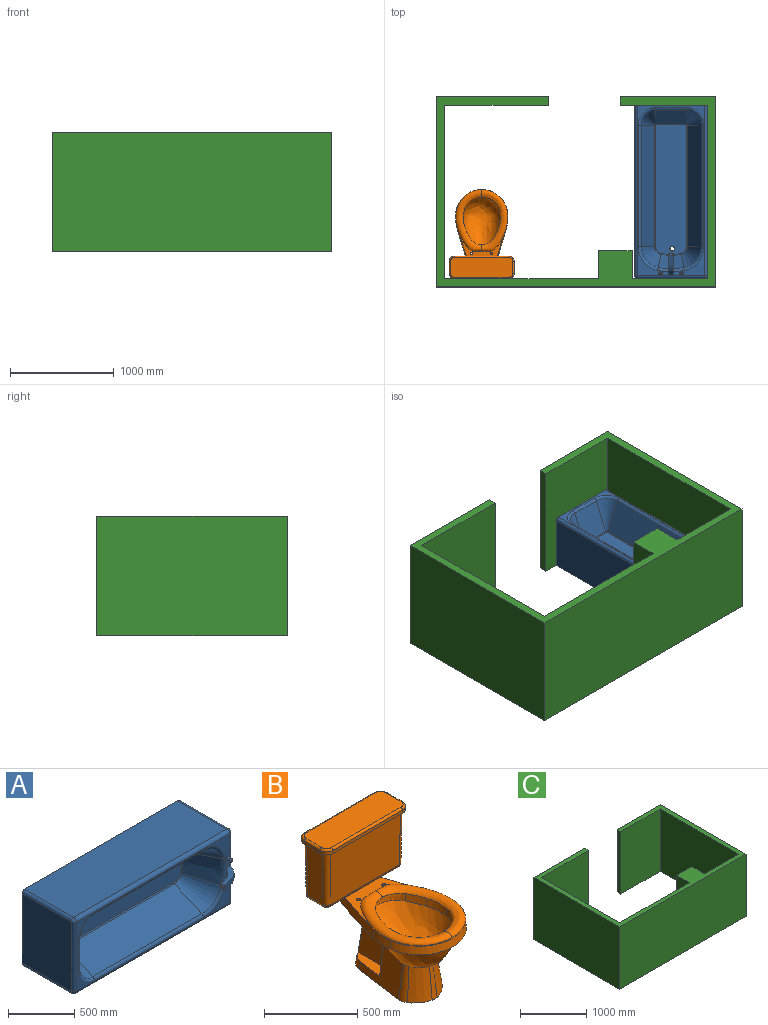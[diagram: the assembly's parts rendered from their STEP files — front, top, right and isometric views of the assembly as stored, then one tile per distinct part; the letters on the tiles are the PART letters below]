
ASSEMBLY  parts=3 mates=5
PART A: 64 faces, bbox 1708.3x711.8x712.6 mm
  f0: plane 1640x640mm, normal (0,-1,0), area 85361.7mm2, adj f16,f17,f18,f19,f20,f21,f22,f23
  f1: plane 51.88x40mm, normal (-0.3,0.95,0), area 1666.8mm2, adj f40,f41,f42,f44,f48
  f2: plane 640x525mm, normal (-1,0,0), area 336000mm2, adj f6,f18,f56,f58
  f3: plane 1640x525mm, normal (0,0,-1), area 861000mm2, adj f6,f16,f56,f62
  f4: plane 640x525mm, normal (1,0,0), area 336000mm2, adj f6,f17,f60,f62
  f5: plane 1640x525mm, normal (0,0,1), area 861000mm2, adj f6,f19,f58,f60
  f6: plane 1700x700mm, normal (0,1,0), area 1187791.8mm2, adj f2,f3,f4,f5,f36,f56,f58,f60
  f7: plane 1249.03x300.79mm, normal (0,-1,0), area 370651mm2, adj f28,f29,f30,f31,f32,f33,f34,f35
  f8: plane 1168.01x296.03mm, normal (0,-0.4,-0.92), area 377412.1mm2, adj f9,f10,f23,f30
  f9: cone r=150mm half-angle=23.6deg, axis (0,-1,0), area 39274.5mm2, adj f8,f15,f25,f28
  f10: cone r=215.58mm half-angle=23.6deg, axis (0,-1,0), area 62922.8mm2, adj f8,f11,f21,f32
  f11: cone r=608.37mm half-angle=23.6deg, axis (0,-1,0), area 72233.3mm2, adj f10,f12,f20,f34
  f12: cone r=215.58mm half-angle=23.6deg, axis (0,-1,0), area 62922.8mm2, adj f11,f13,f22,f35
  f13: plane 1168.01x296.03mm, normal (0,-0.4,0.92), area 377412.1mm2, adj f12,f14,f24,f33
  f14: cone r=150mm half-angle=23.6deg, axis (0,-1,0), area 39274.5mm2, adj f13,f15,f26,f31
  f15: plane 296.03x293.87mm, normal (0.92,-0.4,0), area 94956mm2, adj f9,f14,f27,f29
  f16: cylinder r=30mm len=1640mm, axis (1,0,0), area 77283.2mm2, adj f0,f3,f57,f63
  f17: cylinder r=30mm len=640mm, axis (0,0,1), area 30159.3mm2, adj f0,f4,f37,f61,f63
  f18: cylinder r=30mm len=640mm, axis (0,0,-1), area 30159.3mm2, adj f0,f2,f57,f59
  f19: cylinder r=30mm len=1640mm, axis (-1,0,0), area 77283.2mm2, adj f0,f5,f59,f61
  f20: torus R=627.99mm, axis (0,1,0), area 8881.1mm2, adj f0,f11,f21,f22
  f21: torus R=235.2mm, axis (0,1,0), area 10399.2mm2, adj f0,f10,f20,f23
  f22: torus R=235.2mm, axis (0,1,0), area 10399.2mm2, adj f0,f12,f20,f24
  f23: cylinder r=30mm len=1168.01mm, axis (-1,0,0), area 40590.1mm2, adj f0,f8,f21,f25
  f24: cylinder r=30mm len=1168.01mm, axis (1,0,0), area 40590.1mm2, adj f0,f13,f22,f26
  f25: torus R=169.62mm, axis (0,1,0), area 8412.1mm2, adj f0,f9,f23,f27
  f26: torus R=169.62mm, axis (0,1,0), area 8412.1mm2, adj f0,f14,f24,f27
  f27: cylinder r=30mm len=293.87mm, axis (0,0,-1), area 10212.4mm2, adj f0,f15,f25,f26
  f28: torus R=3.46mm, axis (0,-1,0), area 157.1mm2, adj f7,f9,f29,f30
  f29: cylinder r=10mm len=293.87mm, axis (0,0,-1), area 3404.1mm2, adj f7,f15,f28,f31
  f30: cylinder r=10mm len=1168.01mm, axis (-1,0,0), area 13530mm2, adj f7,f8,f28,f32
  f31: torus R=3.46mm, axis (0,-1,0), area 157.1mm2, adj f7,f14,f29,f33
  f32: torus R=69.04mm, axis (0,-1,0), area 1171mm2, adj f7,f10,f30,f34
  f33: cylinder r=10mm len=1168.01mm, axis (1,0,0), area 13530mm2, adj f7,f13,f31,f35
  f34: torus R=461.83mm, axis (0,-1,0), area 2257.2mm2, adj f7,f11,f32,f35
  f35: torus R=69.04mm, axis (0,-1,0), area 1171mm2, adj f7,f12,f33,f34
  f36: cylinder r=21.38mm len=235mm, axis (0,-1,0), area 31563.9mm2, adj f6,f7
  f37: plane 40x22.85mm, normal (0.97,-0.24,0), area 941.7mm2, adj f17,f40,f41,f43
  f38: plane 97.82x40mm, normal (0.3,-0.95,0), area 4106mm2, adj f40,f41,f43,f47
  f39: plane 20x14.29mm, normal (-0.95,-0.3,0), area 300mm2, adj f44,f45,f46,f47
  f40: plane 207.54x153.77mm, normal (0,0,-1), area 9708.8mm2, adj f0,f1,f37,f38,f42,f43,f45
  f41: plane 207.54x153.77mm, normal (0,0,1), area 9708.8mm2, adj f0,f1,f37,f38,f42,f43,f46
  f42: cylinder r=200mm len=119.6mm, axis (0,0,1), area 6516.3mm2, adj f0,f1,f40,f41
  f43: cylinder r=140mm len=99.8mm, axis (0,0,1), area 5713.6mm2, adj f37,f38,f40,f41
  f44: cylinder r=10mm len=40mm, axis (0,0,1), area 514.2mm2, adj f1,f39,f45,f46
  f45: cylinder r=10mm len=36.38mm, axis (-0.3,0.95,0), area 435.6mm2, adj f39,f40,f44,f47
  f46: cylinder r=10mm len=36.38mm, axis (0.3,-0.95,0), area 435.6mm2, adj f39,f41,f44,f47
  f47: cylinder r=10mm len=40mm, axis (0,0,1), area 514.2mm2, adj f38,f39,f45,f46
  f48: cylinder r=12.75mm len=30.37mm, axis (0.3,-0.95,0), area 1602.5mm2, adj f1,f49
  f49: plane 25.5x24.3mm, normal (-0.3,0.95,0), area 510.9mm2, adj f48
  f50: cylinder r=17.44mm len=34.88mm, axis (0,1,0), area 3286.9mm2, adj f0,f52
  f51: plane 14.88x14.88mm, normal (0,-1,0), area 173.8mm2, adj f52
  f52: torus R=7.44mm, axis (0,-1,0), area 1362.4mm2, adj f50,f51
  f53: cylinder r=17.44mm len=34.88mm, axis (0,1,0), area 3286.9mm2, adj f0,f55
  f54: plane 14.88x14.88mm, normal (0,-1,0), area 173.8mm2, adj f55
  f55: torus R=7.44mm, axis (0,-1,0), area 1362.4mm2, adj f53,f54
  f56: cylinder r=30mm len=525mm, axis (0,1,0), area 24740mm2, adj f2,f3,f6,f57
  f57: sphere r=30mm, area 1413.7mm2, adj f16,f18,f56
  f58: cylinder r=30mm len=525mm, axis (0,1,0), area 24740mm2, adj f2,f5,f6,f59
  f59: sphere r=30mm, area 1413.7mm2, adj f18,f19,f58
  f60: cylinder r=30mm len=525mm, axis (0,1,0), area 24740mm2, adj f4,f5,f6,f61
  f61: sphere r=30mm, area 1413.7mm2, adj f17,f19,f60
  f62: cylinder r=30mm len=525mm, axis (0,1,0), area 24740mm2, adj f3,f4,f6,f63
  f63: sphere r=30mm, area 1413.7mm2, adj f16,f17,f62
PART B: 178 faces, bbox 660.3x888.4x889 mm
  f0: plane 6.63x6.46mm, normal (0,0,-1), area 25mm2, adj f11,f12,f13,f110
  f1: plane 6.43x3.66mm, normal (0,0,-1), area 12.9mm2, adj f18,f108,f109
  f2: plane 6.63x6.46mm, normal (0,0,-1), area 25mm2, adj f28,f29,f30,f110
  f3: plane 6.43x3.66mm, normal (0,0,-1), area 12.9mm2, adj f35,f111,f112
  f4: plane 589.56x500.14mm, normal (0,0,-1), area 105064.3mm2, adj f5,f6,f7,f8,f9,f14,f15,f16
  f5: bspline ~589.56x250.07mm, area 66336.6mm2, adj f4,f22
  f6: plane 29.24x25.8mm, normal (0.66,-0.75,0), area 117mm2, adj f4,f7,f9,f11
  f7: cylinder r=7.5mm len=13.12mm, axis (0,0,1), area 70.7mm2, adj f4,f6,f8,f13
  f8: plane 29.24x25.8mm, normal (-0.66,0.75,0), area 117mm2, adj f4,f7,f9,f12
  f9: cylinder r=7.5mm len=13.12mm, axis (0,0,1), area 70.7mm2, adj f4,f6,f8,f10
  f10: torus R=3.5mm, axis (0,0,1), area 119.4mm2, adj f9,f11,f12,f39
  f11: cylinder r=4mm len=31.89mm, axis (0.75,0.66,0), area 245mm2, adj f0,f6,f10,f13,f39
  f12: cylinder r=4mm len=31.89mm, axis (-0.75,-0.66,0), area 245mm2, adj f0,f8,f10,f13,f39
  f13: torus R=3.5mm, axis (0,0,1), area 119.4mm2, adj f0,f7,f11,f12
  f14: cylinder r=7.5mm len=14.64mm, axis (0,0,1), area 70.7mm2, adj f4,f15,f17,f21
  f15: plane 37.1x12.02mm, normal (0.31,0.95,0), area 117mm2, adj f4,f14,f16,f20
  f16: cylinder r=7.5mm len=14.64mm, axis (0,0,1), area 70.7mm2, adj f4,f15,f17,f18
  f17: plane 37.1x12.02mm, normal (-0.31,-0.95,0), area 117mm2, adj f4,f14,f16,f19
  f18: torus R=3.5mm, axis (0,0,1), area 119.4mm2, adj f1,f16,f19,f20,f39
  f19: cylinder r=4mm len=38.34mm, axis (0.95,-0.31,0), area 245mm2, adj f17,f18,f21,f39
  f20: cylinder r=4mm len=38.34mm, axis (-0.95,0.31,0), area 245mm2, adj f15,f18,f21,f39
  f21: torus R=3.5mm, axis (0,0,1), area 119.4mm2, adj f14,f19,f20,f39
  f22: bspline ~589.56x250.07mm, area 66336.6mm2, adj f4,f5
  f23: plane 29.24x25.8mm, normal (-0.66,-0.75,0), area 117mm2, adj f4,f24,f26,f28
  f24: cylinder r=7.5mm len=13.12mm, axis (0,0,1), area 70.7mm2, adj f4,f23,f25,f30
  f25: plane 29.24x25.8mm, normal (0.66,0.75,0), area 117mm2, adj f4,f24,f26,f29
  f26: cylinder r=7.5mm len=13.12mm, axis (0,0,1), area 70.7mm2, adj f4,f23,f25,f27
  f27: torus R=3.5mm, axis (0,0,1), area 119.4mm2, adj f26,f28,f29,f39
  f28: cylinder r=4mm len=31.89mm, axis (-0.75,0.66,0), area 245mm2, adj f2,f23,f27,f30,f39
  f29: cylinder r=4mm len=31.89mm, axis (0.75,-0.66,0), area 245mm2, adj f2,f25,f27,f30,f39
  f30: torus R=3.5mm, axis (0,0,1), area 119.4mm2, adj f2,f24,f28,f29
  f31: cylinder r=7.5mm len=14.64mm, axis (0,0,1), area 70.7mm2, adj f4,f32,f34,f38
  f32: plane 37.1x12.02mm, normal (-0.31,0.95,0), area 117mm2, adj f4,f31,f33,f37
  f33: cylinder r=7.5mm len=14.64mm, axis (0,0,1), area 70.7mm2, adj f4,f32,f34,f35
  f34: plane 37.1x12.02mm, normal (0.31,-0.95,0), area 117mm2, adj f4,f31,f33,f36
  f35: torus R=3.5mm, axis (0,0,1), area 119.4mm2, adj f3,f33,f36,f37,f39
  f36: cylinder r=4mm len=38.34mm, axis (-0.95,-0.31,0), area 245mm2, adj f34,f35,f38,f39
  f37: cylinder r=4mm len=38.34mm, axis (0.95,0.31,0), area 245mm2, adj f32,f35,f38,f39
  f38: torus R=3.5mm, axis (0,0,1), area 119.4mm2, adj f31,f36,f37,f39
  f39: plane 682.07x486.65mm, normal (0,0,1), area 110534.9mm2, adj f10,f11,f12,f18,f19,f20,f21,f27
  f40: plane 601.26x191.84mm, normal (0,0,-1), area 7653mm2, adj f50,f51,f52,f53,f54,f55,f56,f57
  f41: cylinder r=49.83mm len=49.83mm, axis (0,0,1), area 1491.1mm2, adj f42,f48,f49,f65
  f42: plane 117.58x19.05mm, normal (-1,0,0), area 2239.9mm2, adj f41,f43,f49,f66
  f43: cylinder r=49.83mm len=49.83mm, axis (0,0,1), area 1491.1mm2, adj f42,f44,f49,f64
  f44: plane 527x19.05mm, normal (0,1,0), area 10039.4mm2, adj f43,f45,f49,f62
  f45: cylinder r=49.83mm len=49.83mm, axis (0,0,1), area 1491.1mm2, adj f44,f46,f49,f60
  f46: plane 117.58x19.05mm, normal (1,0,0), area 2239.9mm2, adj f45,f47,f49,f59
  f47: cylinder r=49.83mm len=49.83mm, axis (0,0,1), area 1491.1mm2, adj f46,f48,f49,f61
  f48: plane 527x19.05mm, normal (0,-1,0), area 10039.4mm2, adj f41,f47,f49,f63
  f49: plane 626.66x217.24mm, normal (0,0,-1), area 19842mm2, adj f41,f42,f43,f44,f45,f46,f47,f48
  f50: cylinder r=37.13mm len=37.13mm, axis (0,0,1), area 370.4mm2, adj f40,f49,f51,f57
  f51: plane 117.58x6.35mm, normal (-1,0,0), area 746.6mm2, adj f40,f49,f50,f52
  f52: cylinder r=37.13mm len=37.13mm, axis (0,0,1), area 370.4mm2, adj f40,f49,f51,f53
  f53: plane 527x6.35mm, normal (0,1,0), area 3346.5mm2, adj f40,f49,f52,f54
  f54: cylinder r=37.13mm len=37.13mm, axis (0,0,1), area 370.4mm2, adj f40,f49,f53,f55
  f55: plane 117.58x6.35mm, normal (1,0,0), area 746.6mm2, adj f40,f49,f54,f56
  f56: cylinder r=37.13mm len=37.13mm, axis (0,0,1), area 370.4mm2, adj f40,f49,f55,f57
  f57: plane 527x6.35mm, normal (0,-1,0), area 3346.5mm2, adj f40,f49,f50,f56
  f58: plane 601.26x191.84mm, normal (0,0,1), area 114163.7mm2, adj f59,f60,f61,f62,f63,f64,f65,f66
  f59: cylinder r=12.7mm len=117.58mm, axis (0,-1,0), area 2345.6mm2, adj f46,f58,f60,f61
  f60: torus R=37.13mm, axis (0,0,1), area 1416.9mm2, adj f45,f58,f59,f62
  f61: torus R=37.13mm, axis (0,0,1), area 1416.9mm2, adj f47,f58,f59,f63
  f62: cylinder r=12.7mm len=527mm, axis (1,0,0), area 10513.2mm2, adj f44,f58,f60,f64
  f63: cylinder r=12.7mm len=527mm, axis (-1,0,0), area 10513.2mm2, adj f48,f58,f61,f65
  f64: torus R=37.13mm, axis (0,0,1), area 1416.9mm2, adj f43,f58,f62,f66
  f65: torus R=37.13mm, axis (0,0,1), area 1416.9mm2, adj f41,f58,f63,f66
  f66: cylinder r=12.7mm len=117.58mm, axis (0,1,0), area 2345.6mm2, adj f42,f58,f64,f65
  f67: plane 26.5x26.5mm, normal (0,0,-1), area 551.7mm2, adj f69
  f68: plane 26.5x26.5mm, normal (0,0,-1), area 551.7mm2, adj f70
  f69: cylinder r=13.25mm len=31.7mm, axis (0,0,1), area 1450.3mm2, adj f67,f102,f103,f127
  f70: cylinder r=13.25mm len=31.7mm, axis (0,0,1), area 1450.6mm2, adj f68,f105,f106,f127
  f71: cylinder r=11.96mm len=23.92mm, axis (0,0,1), area 954.4mm2, adj f39,f127
  f72: cylinder r=11.96mm len=23.92mm, axis (0,0,1), area 954.4mm2, adj f39,f127
  f73: plane 203.2x38.1mm, normal (0.71,0.71,0), area 10948.7mm2, adj f74,f75,f76,f77
  f74: plane 237.76x74.36mm, normal (0,0,1), area 12302.8mm2, adj f73,f76,f77,f131,f132
  f75: plane 204.52x45.54mm, normal (0,0,-1), area 5536.8mm2, adj f73,f76,f77,f131,f132
  f76: plane 203.2x36.26mm, normal (0,1,0), area 4439.1mm2, adj f73,f74,f75,f131
  f77: plane 207.01x203.47mm, normal (1,0,0), area 37269.3mm2, adj f73,f74,f75,f132
  f78: plane 203.2x38.1mm, normal (-0.71,0.71,0), area 10948.7mm2, adj f79,f80,f81,f82
  f79: plane 237.76x74.36mm, normal (0,0,1), area 12302.8mm2, adj f78,f81,f82,f130,f132
  f80: plane 204.52x45.54mm, normal (0,0,-1), area 5536.8mm2, adj f78,f81,f82,f130,f132
  f81: plane 207.01x203.47mm, normal (-1,0,0), area 37269.3mm2, adj f78,f79,f80,f132
  f82: plane 203.2x36.26mm, normal (0,1,0), area 4439.1mm2, adj f78,f79,f80,f130
  f83: plane 560.3x287.95mm, normal (0,0,-1), area 123539mm2, adj f84,f85,f86,f87,f88,f130,f131,f132
  f84: cone r=76.2mm half-angle=8deg, axis (0,0,-1), area 10378.2mm2, adj f83,f85,f126,f131
  f85: cone r=197.74mm half-angle=8deg, axis (0,0,-1), area 27185.8mm2, adj f83,f84,f86,f126
  f86: cone r=76.2mm half-angle=8deg, axis (0,0,-1), area 6573mm2, adj f83,f85,f87,f126
  f87: cone r=197.74mm half-angle=8deg, axis (0,0,-1), area 27152.3mm2, adj f83,f86,f88,f126
  f88: cone r=76.2mm half-angle=8deg, axis (0,0,-1), area 10372.1mm2, adj f83,f87,f126,f130
  f89: offset ~583.11x463.72mm, area 264467.6mm2, adj f90,f91,f92,f93,f94,f95
  f90: cylinder r=337.73mm len=141.19mm, axis (0,0,1), area 601mm2, adj f89,f91,f95,f114
  f91: cylinder r=970.9mm len=115.37mm, axis (0,0,1), area 405.1mm2, adj f89,f90,f92,f114
  f92: cylinder r=148.33mm len=268.25mm, axis (0,0,1), area 940.7mm2, adj f89,f91,f93,f114
  f93: cylinder r=970.9mm len=115.37mm, axis (0,0,1), area 397.7mm2, adj f89,f92,f94,f114
  f94: cylinder r=337.73mm len=141.19mm, axis (0,0,1), area 570.6mm2, adj f89,f93,f95,f114
  f95: cylinder r=195.4mm len=388.44mm, axis (0,0,1), area 2589.6mm2, adj f89,f90,f94,f114
  f96: cylinder r=208.1mm len=413.69mm, axis (0,0,1), area 3860.1mm2, adj f97,f100,f123,f126
  f97: cylinder r=350.43mm len=146.5mm, axis (0,0,1), area 942.1mm2, adj f96,f98,f123,f126
  f98: cylinder r=983.6mm len=116.88mm, axis (0,0,1), area 798.9mm2, adj f97,f123,f125,f126
  f99: cylinder r=983.6mm len=116.88mm, axis (0,0,1), area 798.9mm2, adj f100,f123,f124,f126
  f100: cylinder r=350.43mm len=146.5mm, axis (0,0,1), area 942.2mm2, adj f96,f99,f123,f126
  f101: plane 38.43x32.77mm, normal (0,0.93,-0.36), area 737mm2, adj f102,f123,f127,f129
  f102: cone r=3586.69mm half-angle=21deg, axis (0,0,-1), area 10140.2mm2, adj f69,f101,f103,f123,f127
  f103: cone r=88.16mm half-angle=21deg, axis (0,0,-1), area 3307.5mm2, adj f69,f102,f104,f123,f127
  f104: cone r=218.65mm half-angle=21deg, axis (0,0,-1), area 1626.9mm2, adj f103,f105,f123,f127
  f105: cone r=88.16mm half-angle=21deg, axis (0,0,-1), area 3307.9mm2, adj f70,f104,f106,f123,f127
  f106: cone r=3586.69mm half-angle=21deg, axis (0,0,-1), area 10140.2mm2, adj f70,f105,f107,f123,f127
  f107: plane 38.43x32.77mm, normal (0,0.93,-0.36), area 737mm2, adj f106,f123,f127,f128
  f108: cone r=967.16mm half-angle=10deg, axis (0,0,1), area 6351.6mm2, adj f1,f39,f109,f113,f114
  f109: cone r=333.99mm half-angle=10deg, axis (0,0,1), area 7196.3mm2, adj f1,f39,f108,f110,f114
  f110: cone r=191.66mm half-angle=10deg, axis (0,0,1), area 28206.9mm2, adj f0,f2,f39,f109,f111,f114
  f111: cone r=333.99mm half-angle=10deg, axis (0,0,1), area 7196.3mm2, adj f3,f39,f110,f112,f114
  f112: cone r=967.16mm half-angle=10deg, axis (0,0,1), area 6351.6mm2, adj f3,f39,f111,f113,f114
  f113: cone r=144.58mm half-angle=10deg, axis (0,0,1), area 16328.2mm2, adj f39,f108,f112,f114
  f114: plane 515.49x392.53mm, normal (0,0,-1), area 17785mm2, adj f90,f91,f92,f93,f94,f95,f108,f109
  f115: cone r=235.09mm half-angle=10deg, axis (0,0,-1), area 2331.5mm2, adj f116,f122,f123,f135
  f116: cone r=104.6mm half-angle=10deg, axis (0,0,-1), area 6259.1mm2, adj f115,f117,f123,f135,f150
  f117: cone r=3603.13mm half-angle=10deg, axis (0,0,-1), area 20573.2mm2, adj f39,f116,f118,f123,f150
  f118: cone r=384.79mm half-angle=10deg, axis (0,0,-1), area 7301.9mm2, adj f39,f117,f119,f123
  f119: cone r=242.46mm half-angle=10deg, axis (0,0,-1), area 37211.9mm2, adj f39,f118,f120,f123
  f120: cone r=384.79mm half-angle=10deg, axis (0,0,-1), area 7301.9mm2, adj f39,f119,f121,f123
  f121: cone r=3603.13mm half-angle=10deg, axis (0,0,-1), area 20573.2mm2, adj f39,f120,f122,f123,f141
  f122: cone r=104.6mm half-angle=10deg, axis (0,0,-1), area 6259.2mm2, adj f115,f121,f123,f135,f141
  f123: plane 819.76x504.56mm, normal (0,0,-1), area 74259.2mm2, adj f96,f97,f98,f99,f100,f101,f102,f103
  f124: cylinder r=161.03mm len=102.27mm, axis (0,0,1), area 873.4mm2, adj f99,f126,f128,f131
  f125: cylinder r=161.03mm len=102.27mm, axis (0,0,1), area 873.4mm2, adj f98,f126,f129,f130
  f126: bspline ~557.71x438.33mm, area 217099mm2, adj f84,f85,f86,f87,f88,f96,f97,f98
  f127: plane 316.67x273.18mm, normal (0,0,-1), area 36562.5mm2, adj f69,f70,f71,f72,f101,f102,f103,f104
  f128: cone r=161.03mm half-angle=21deg, axis (0,0,1), area 5939.9mm2, adj f107,f124,f127,f131
  f129: cone r=161.03mm half-angle=21deg, axis (0,0,1), area 5939.9mm2, adj f101,f125,f127,f130
  f130: plane 445.06x347.95mm, normal (-0.98,0.13,0.14), area 70082.7mm2, adj f79,f80,f82,f83,f88,f125,f126,f127
  f131: plane 445.06x348.01mm, normal (0.98,0.13,0.14), area 69662.7mm2, adj f74,f75,f76,f83,f84,f124,f126,f127
  f132: cone r=97.69mm half-angle=8deg, axis (0,0,-1), area 57658.1mm2, adj f74,f75,f77,f79,f80,f81,f83,f127
  f133: torus R=0.44mm, axis (0,0,1), area 1023mm2, adj f134,f135,f145,f150
  f134: cylinder r=25.4mm len=117.58mm, axis (0,1,0), area 4639.1mm2, adj f133,f136,f144,f150
  f135: cylinder r=25.4mm len=527mm, axis (1,0,0), area 20749.3mm2, adj f115,f116,f122,f133,f137,f141,f146,f150
  f136: torus R=0.44mm, axis (0,0,1), area 1023mm2, adj f134,f138,f143,f150
  f137: torus R=0.44mm, axis (0,0,1), area 1023mm2, adj f135,f139,f141,f147
  f138: cylinder r=25.4mm len=527mm, axis (-1,0,0), area 20792.8mm2, adj f39,f136,f140,f141,f142,f150
  f139: cylinder r=25.4mm len=117.58mm, axis (0,-1,0), area 4639.1mm2, adj f137,f140,f141,f148
  f140: torus R=0.44mm, axis (0,0,1), area 1023mm2, adj f138,f139,f141,f149
  f141: plane 239.27x118.47mm, normal (0,0,-1), area 19463.9mm2, adj f121,f122,f135,f137,f138,f139,f140
  f142: plane 527x356.04mm, normal (0,-1,-0.02), area 187664.1mm2, adj f40,f138,f143,f149
  f143: cone r=25.4mm half-angle=1deg, axis (0,0,1), area 16189.5mm2, adj f40,f136,f142,f144
  f144: plane 356.04x117.58mm, normal (-1,0,-0.02), area 41870.2mm2, adj f40,f134,f143,f145
  f145: cone r=25.4mm half-angle=1deg, axis (0,0,1), area 16189.5mm2, adj f40,f133,f144,f146
  f146: plane 527x356.04mm, normal (0,1,-0.02), area 187664.1mm2, adj f40,f135,f145,f147
  f147: cone r=25.4mm half-angle=1deg, axis (0,0,1), area 16189.5mm2, adj f40,f137,f146,f148
  f148: plane 356.04x117.58mm, normal (1,0,-0.02), area 41870.2mm2, adj f40,f139,f147,f149
  f149: cone r=25.4mm half-angle=1deg, axis (0,0,1), area 16189.5mm2, adj f40,f140,f142,f148
  f150: plane 239.27x118.47mm, normal (0,0,-1), area 19464mm2, adj f116,f117,f133,f134,f135,f136,f138
  f151: plane 588.56x179.14mm, normal (0,0,-1), area 104622.7mm2, adj f152,f153,f154,f155,f156,f157,f158,f159
  f152: plane 527x12.7mm, normal (0,-1,0), area 6692.9mm2, adj f151,f153,f159,f160
  f153: cylinder r=30.78mm len=30.78mm, axis (0,0,-1), area 614mm2, adj f151,f152,f154,f160
  f154: plane 117.58x12.7mm, normal (1,0,0), area 1493.3mm2, adj f151,f153,f155,f160
  f155: cylinder r=30.78mm len=30.78mm, axis (0,0,-1), area 614mm2, adj f151,f154,f156,f160
  f156: plane 527x12.7mm, normal (0,1,0), area 6692.9mm2, adj f151,f155,f157,f160
  f157: cylinder r=30.78mm len=30.78mm, axis (0,0,-1), area 614mm2, adj f151,f156,f158,f160
  f158: plane 117.58x12.7mm, normal (-1,0,0), area 1493.3mm2, adj f151,f157,f159,f160
  f159: cylinder r=30.78mm len=30.78mm, axis (0,0,-1), area 614mm2, adj f151,f152,f158,f160
  f160: plane 588.56x179.14mm, normal (0,0,1), area 16538mm2, adj f152,f153,f154,f155,f156,f157,f158,f159
  f161: cone r=12.7mm half-angle=1deg, axis (0,0,1), area 9080mm2, adj f160,f162,f168,f170
  f162: plane 355.82x117.58mm, normal (-1,0,0.02), area 41844.2mm2, adj f160,f161,f163,f171
  f163: cone r=12.7mm half-angle=1deg, axis (0,0,1), area 9080mm2, adj f160,f162,f164,f173
  f164: plane 527x355.82mm, normal (0,-1,0.02), area 187547.2mm2, adj f160,f163,f165,f175
  f165: cone r=12.7mm half-angle=1deg, axis (0,0,1), area 9080mm2, adj f160,f164,f166,f177
  f166: plane 355.82x117.58mm, normal (1,0,0.02), area 41844.2mm2, adj f160,f165,f167,f176
  f167: cone r=12.7mm half-angle=1deg, axis (0,0,1), area 9080mm2, adj f160,f166,f168,f174
  f168: plane 527x355.82mm, normal (0,1,0.02), area 187547.2mm2, adj f160,f161,f167,f172
  f169: plane 527.88x118.46mm, normal (0,0,1), area 62532.5mm2, adj f170,f171,f172,f173,f174,f175,f176,f177
  f170: torus R=0.44mm, axis (0,0,1), area 262.6mm2, adj f161,f169,f171,f172
  f171: cylinder r=12.7mm len=117.58mm, axis (0,-1,0), area 2319.6mm2, adj f162,f169,f170,f173
  f172: cylinder r=12.7mm len=527mm, axis (-1,0,0), area 10396.4mm2, adj f168,f169,f170,f174
  f173: torus R=0.44mm, axis (0,0,1), area 262.6mm2, adj f163,f169,f171,f175
  f174: torus R=0.44mm, axis (0,0,1), area 262.6mm2, adj f167,f169,f172,f176
  f175: cylinder r=12.7mm len=527mm, axis (1,0,0), area 10396.4mm2, adj f164,f169,f173,f177
  f176: cylinder r=12.7mm len=117.58mm, axis (0,1,0), area 2319.6mm2, adj f166,f169,f174,f177
  f177: torus R=0.44mm, axis (0,0,1), area 262.6mm2, adj f165,f169,f175,f176
PART C: 18 faces, bbox 2690x1830x1150 mm
  f0: plane 1670x1150mm, normal (1,0,0), area 1920500mm2, adj f1,f15,f16,f17
  f1: plane 1150x1000mm, normal (0,-1,0), area 1150000mm2, adj f0,f2,f16,f17
  f2: plane 1150x80mm, normal (1,0,0), area 92000mm2, adj f1,f3,f16,f17
  f3: plane 1150x1080mm, normal (0,1,0), area 1242000mm2, adj f2,f4,f16,f17
  f4: plane 1830x1150mm, normal (-1,0,0), area 2104500mm2, adj f3,f5,f16,f17
  f5: plane 2690x1150mm, normal (0,-1,0), area 3093500mm2, adj f4,f6,f16,f17
  f6: plane 1830x1150mm, normal (1,0,0), area 2104500mm2, adj f5,f7,f16,f17
  f7: plane 1150x920mm, normal (0,1,0), area 1058000mm2, adj f6,f8,f16,f17
  f8: plane 1150x80mm, normal (-1,0,0), area 92000mm2, adj f7,f9,f16,f17
  f9: plane 1150x840mm, normal (0,-1,0), area 966000mm2, adj f8,f10,f16,f17
  f10: plane 1670x1150mm, normal (-1,0,0), area 1920500mm2, adj f9,f11,f16,f17
  f11: plane 1150x725mm, normal (0,1,0), area 833750mm2, adj f10,f12,f16,f17
  f12: plane 1150x270mm, normal (1,0,0), area 310500mm2, adj f11,f13,f16,f17
  f13: plane 1150x325mm, normal (0,1,0), area 373750mm2, adj f12,f14,f16,f17
  f14: plane 1150x270mm, normal (-1,0,0), area 310500mm2, adj f13,f15,f16,f17
  f15: plane 1480x1150mm, normal (0,1,0), area 1702000mm2, adj f0,f14,f16,f17
  f16: plane 2690x1830mm, normal (0,0,1), area 730150mm2, adj f0,f1,f2,f3,f4,f5,f6,f7
  f17: plane 2690x1830mm, normal (0,0,-1), area 730150mm2, adj f0,f1,f2,f3,f4,f5,f6,f7
PLACE A rot(axis=(-0.58,0.58,-0.58),120deg) t=(565,865,0)mm
PLACE B rot(axis=(0,0,1),180deg) t=(-907.39,-206.68,457.2)mm
PLACE C at identity fixed
MATE planar B.f44 <-> C.f15  axis (0,-1,0) through (-907.39,-835,841.38)mm
MATE planar B.f83 <-> C.f17  axis (0,0,-1) through (-907.39,-374.58,0)mm
MATE planar A.f6 <-> C.f17  axis (0,0,-1) through (914.99,15.68,0)mm
MATE planar A.f4 <-> C.f15  axis (0,-1,0) through (915,-835,262.5)mm
MATE planar A.f5 <-> C.f10  axis (1,0,0) through (1265,15,262.5)mm
